# Revit family: Seat-LaZBoy-Kadia_Mod_Visitor_Seating-KAM10H
name_source: partatom
category: Furniture
revit_build: Autodesk Revit 2017 (Build: 20160225_1515(x64)
units: mm (PartAtom-declared; Revit-internal decimal feet)

## family parameters
Always vertical = Yes
Cut with Voids When Loaded = No
OmniClass Number = 23.40.20.00
OmniClass Title = General Furniture and Specialties
Room Calculation Point = No
Shared = No
Work Plane-Based = No

## types (3) — shared parameters
Assembly Code = E2020200
Depth = 28.50"
Height = 45.50"
Manufacturer = LaZBoy
Product Documentation Link = URL
URL = https://www.la-z-boy.com
Width = 24.50"

## per-type parameters (varying)
| type | Description | Model |
| Wood Arm Caps | High Back Guest Chair with Arm Wood Arm Caps | KAM10HW |
| Urethane Arm Caps | High Back Guest Chair with Arm Urethane Arm Caps | KAM10HU |
| Solid Surface Arm Caps | High Back Guest Chair with Solid Surface Arm Caps | KAM10HJ |

## geometry (parser evidence)
native form markers: Sweep x3
no freeform markers — native parametric forms only
